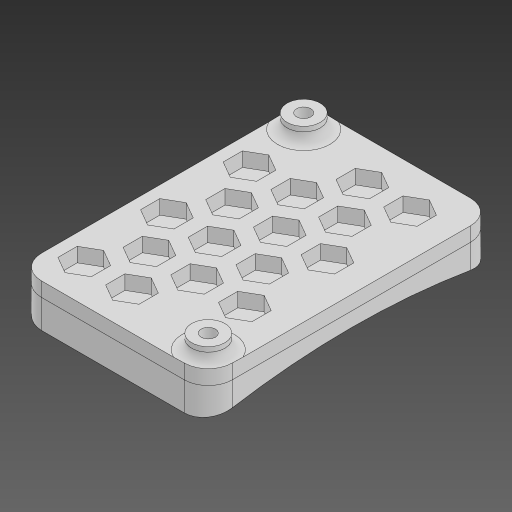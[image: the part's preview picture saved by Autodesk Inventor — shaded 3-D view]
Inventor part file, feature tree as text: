
AUTODESK INVENTOR PART (.ipt)
format: ipt  version: 2023.2 (Build 272271000, 271)  size: 470,016 bytes
history: native  units: mm
features: sketch x5, extrude x5, fillet x3, other x2, hole x1, projected_geometry x1
ambient origin geometry x8: Origin, YZ Plane, XZ Plane, XY Plane, X Axis, Y Axis, Z Axis, Center Point
bodies: Body1 (feature_tree), Body2 (feature_tree)
feature tree (17):
  other  "PCB base"
  sketch  "Sketch1"  dims[d0=60.0mm d1=40.0mm]
  extrude  "Extrusion1"  Depth=40.0mm
  hole  "Hole1"  [1 undecoded]
  extrude  "Extrusion2"  Depth=5.0mm
  fillet  "Fillet1"  Radius=3.0mm
  fillet  "Fillet2"  Radius=2.0mm
  extrude  "Extrusion3"  Depth=10.0mm TaperAngle=0.0deg
  fillet  "Fillet3"  Radius=2.0mm
  extrude  "Extrusion4"  Depth=5.0mm
  extrude  "Extrusion5"  Depth=10.0mm
  sketch  "Sketch2"  dims[d2=5.0mm d3=5.0mm]
  projected_geometry  "Projected Loop1"
  sketch  "Sketch3"  dims[d4=5.0mm d5=5.0mm d6=3.0mm d7=0.0mm]
  other  "Hand"
  sketch  "Sketch4"  dims[d8=3.0mm d9=6.0mm d10=4.0mm d11=2.0mm d12=90.0deg d13=12.0mm d14=20.594885mm d15=2.0mm]
  sketch  "Sketch5"  dims[d16=2.0mm d17=3.0mm d18=0.0mm d19=2.0mm d20=5.0mm d21=6.0mm d22=3.0mm d23=40.0mm d24=0.0mm d25=5.0mm d26=40.0mm d27=0.0mm d28=7.0mm d29=6.0mm d30=8.0mm d31=50.0mm d33=10.0mm d34=70.0mm d36=10.0mm d39=50.0mm d41=10.0mm d42=70.0mm d44=10.0mm d47=3.0mm d48=0.0mm]
note: 1 required parameter value undecoded (feature->parameter linkage not recoverable at this tier; creation-order binding heuristic only, values carry confidence <= 0.55)
